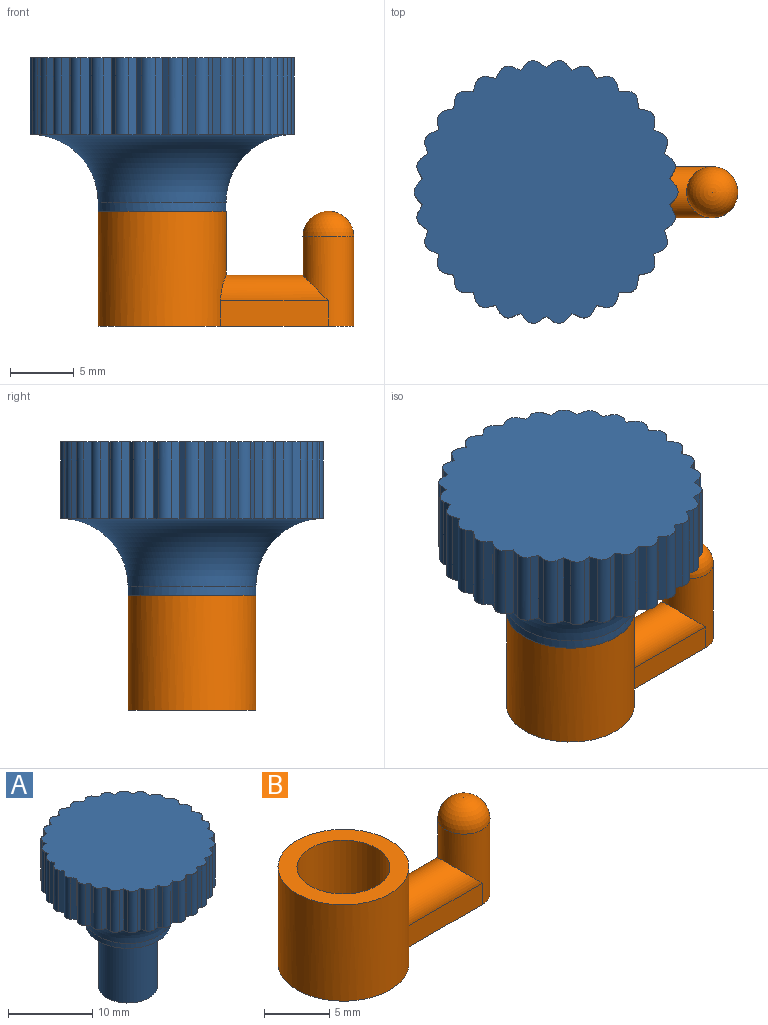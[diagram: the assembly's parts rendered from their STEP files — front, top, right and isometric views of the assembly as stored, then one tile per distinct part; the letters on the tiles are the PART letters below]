
ASSEMBLY  parts=2 mates=1
PART A: 133 faces, bbox 30.5x30.5x21 mm
  f0: cylinder r=5mm len=10mm, axis (0,0,-1), area 22mm2, adj f92,f93
  f1: plane 0.36x0.16mm, normal (0,0,-1), area 0mm2, adj f92,f122
  f2: plane 0.39x0.08mm, normal (0,0,-1), area 0mm2, adj f92,f123
  f3: plane 0.4x0.03mm, normal (0,0,-1), area 0mm2, adj f92,f124
  f4: plane 0.39x0.08mm, normal (0,0,-1), area 0mm2, adj f92,f125
  f5: plane 0.36x0.16mm, normal (0,0,-1), area 0mm2, adj f92,f126
  f6: plane 0.32x0.23mm, normal (0,0,-1), area 0mm2, adj f92,f127
  f7: plane 0.3x0.27mm, normal (0,0,-1), area 0mm2, adj f92,f128
  f8: plane 0.34x0.2mm, normal (0,0,-1), area 0mm2, adj f92,f129
  f9: plane 0.38x0.12mm, normal (0,0,-1), area 0mm2, adj f92,f130
  f10: plane 0.4x0.05mm, normal (0,0,-1), area 0mm2, adj f92,f131
  f11: plane 0.4x0.05mm, normal (0,0,-1), area 0mm2, adj f92,f132
  f12: plane 0.38x0.12mm, normal (0,0,-1), area 0mm2, adj f92,f103
  f13: plane 0.34x0.2mm, normal (0,0,-1), area 0mm2, adj f92,f104
  f14: plane 0.3x0.27mm, normal (0,0,-1), area 0mm2, adj f92,f105
  f15: plane 0.32x0.23mm, normal (0,0,-1), area 0mm2, adj f92,f106
  f16: plane 0.36x0.16mm, normal (0,0,-1), area 0mm2, adj f92,f107
  f17: plane 0.39x0.08mm, normal (0,0,-1), area 0mm2, adj f92,f108
  f18: plane 0.4x0.03mm, normal (0,0,-1), area 0mm2, adj f92,f109
  f19: plane 0.39x0.08mm, normal (0,0,-1), area 0mm2, adj f92,f110
  f20: plane 0.36x0.16mm, normal (0,0,-1), area 0mm2, adj f92,f111
  f21: plane 0.32x0.23mm, normal (0,0,-1), area 0mm2, adj f92,f112
  f22: plane 0.3x0.27mm, normal (0,0,-1), area 0mm2, adj f92,f113
  f23: plane 0.34x0.2mm, normal (0,0,-1), area 0mm2, adj f92,f114
  f24: plane 0.38x0.12mm, normal (0,0,-1), area 0mm2, adj f92,f115
  f25: plane 0.4x0.05mm, normal (0,0,-1), area 0mm2, adj f92,f116
  f26: plane 0.4x0.05mm, normal (0,0,-1), area 0mm2, adj f92,f117
  f27: plane 0.38x0.12mm, normal (0,0,-1), area 0mm2, adj f92,f118
  f28: plane 0.34x0.2mm, normal (0,0,-1), area 0mm2, adj f92,f119
  f29: plane 0.3x0.27mm, normal (0,0,-1), area 0mm2, adj f92,f120
  f30: plane 6.04x0.5mm, normal (-0.75,0.66,0), area 3.9mm2, adj f31,f90,f92,f132
  f31: plane 6.04x0.6mm, normal (0.42,0.91,0), area 3.9mm2, adj f30,f90,f92,f103
  f32: plane 6.04x0.57mm, normal (-0.87,0.49,0), area 3.9mm2, adj f33,f90,f92,f103
  f33: plane 6.04x0.64mm, normal (0.22,0.98,0), area 3.9mm2, adj f32,f90,f92,f104
  f34: plane 6.04x0.63mm, normal (-0.95,0.3,0), area 3.9mm2, adj f35,f90,f92,f104
  f35: plane 6.04x0.66mm, normal (0.01,1,0), area 3.9mm2, adj f34,f90,f92,f105
  f36: plane 6.04x0.65mm, normal (-1,0.09,0), area 3.9mm2, adj f37,f90,f92,f105
  f37: plane 6.04x0.65mm, normal (-0.2,0.98,0), area 3.9mm2, adj f36,f90,f92,f106
  f38: plane 6.04x0.65mm, normal (-0.99,-0.12,0), area 3.9mm2, adj f39,f90,f92,f106
  f39: plane 6.04x0.6mm, normal (-0.4,0.92,0), area 3.9mm2, adj f38,f90,f92,f107
  f40: plane 6.04x0.62mm, normal (-0.95,-0.32,0), area 3.9mm2, adj f41,f90,f92,f107
  f41: plane 6.04x0.54mm, normal (-0.58,0.82,0), area 3.9mm2, adj f40,f90,f92,f108
  f42: plane 6.04x0.57mm, normal (-0.86,-0.51,0), area 3.9mm2, adj f43,f90,f92,f108
  f43: plane 6.04x0.49mm, normal (-0.74,0.68,0), area 3.9mm2, adj f42,f90,f92,f109
  f44: plane 6.04x0.49mm, normal (-0.74,-0.68,0), area 3.9mm2, adj f45,f90,f92,f109
  f45: plane 6.04x0.57mm, normal (-0.86,0.51,0), area 3.9mm2, adj f44,f90,f92,f110
  f46: plane 6.04x0.54mm, normal (-0.58,-0.82,0), area 3.9mm2, adj f47,f90,f92,f110
  f47: plane 6.04x0.62mm, normal (-0.95,0.32,0), area 3.9mm2, adj f46,f90,f92,f111
  f48: plane 6.04x0.6mm, normal (-0.4,-0.92,0), area 3.9mm2, adj f49,f90,f92,f111
  f49: plane 6.04x0.65mm, normal (-0.99,0.12,0), area 3.9mm2, adj f48,f90,f92,f112
  f50: plane 6.04x0.65mm, normal (-0.2,-0.98,0), area 3.9mm2, adj f51,f90,f92,f112
  f51: plane 6.04x0.65mm, normal (-1,-0.09,0), area 3.9mm2, adj f50,f90,f92,f113
  f52: plane 6.04x0.66mm, normal (0.01,-1,0), area 3.9mm2, adj f53,f90,f92,f113
  f53: plane 6.04x0.63mm, normal (-0.95,-0.3,0), area 3.9mm2, adj f52,f90,f92,f114
  f54: plane 6.04x0.64mm, normal (0.22,-0.98,0), area 3.9mm2, adj f55,f90,f92,f114
  f55: plane 6.04x0.57mm, normal (-0.87,-0.49,0), area 3.9mm2, adj f54,f90,f92,f115
  f56: plane 6.04x0.6mm, normal (0.42,-0.91,0), area 3.9mm2, adj f57,f90,f92,f115
  f57: plane 6.04x0.5mm, normal (-0.75,-0.66,0), area 3.9mm2, adj f56,f90,f92,f116
  f58: plane 6.04x0.53mm, normal (0.6,-0.8,0), area 3.9mm2, adj f59,f90,f92,f116
  f59: plane 6.04x0.53mm, normal (-0.6,-0.8,0), area 3.9mm2, adj f58,f90,f92,f117
  f60: plane 6.04x0.5mm, normal (0.75,-0.66,0), area 3.9mm2, adj f61,f90,f92,f117
  f61: plane 6.04x0.6mm, normal (-0.42,-0.91,0), area 3.9mm2, adj f60,f90,f92,f118
  f62: plane 6.04x0.57mm, normal (0.87,-0.49,0), area 3.9mm2, adj f63,f90,f92,f118
  f63: plane 6.04x0.64mm, normal (-0.22,-0.98,0), area 3.9mm2, adj f62,f90,f92,f119
  f64: plane 6.04x0.63mm, normal (0.95,-0.3,0), area 3.9mm2, adj f65,f90,f92,f119
  f65: plane 6.04x0.66mm, normal (-0.01,-1,0), area 3.9mm2, adj f64,f90,f92,f120
  f66: plane 6.04x0.65mm, normal (1,-0.09,0), area 3.9mm2, adj f67,f90,f92,f120
  f67: plane 6.04x0.65mm, normal (0.2,-0.98,0), area 3.9mm2, adj f66,f90,f92,f121
  f68: plane 6.04x0.65mm, normal (0.99,0.12,0), area 3.9mm2, adj f69,f90,f92,f121
  f69: plane 6.04x0.6mm, normal (0.4,-0.92,0), area 3.9mm2, adj f68,f90,f92,f122
  f70: plane 6.04x0.62mm, normal (0.95,0.32,0), area 3.9mm2, adj f71,f90,f92,f122
  f71: plane 6.04x0.54mm, normal (0.58,-0.82,0), area 3.9mm2, adj f70,f90,f92,f123
  f72: plane 6.04x0.57mm, normal (0.86,0.51,0), area 3.9mm2, adj f73,f90,f92,f123
  f73: plane 6.04x0.49mm, normal (0.74,-0.68,0), area 3.9mm2, adj f72,f90,f92,f124
  f74: plane 6.04x0.49mm, normal (0.74,0.68,0), area 3.9mm2, adj f75,f90,f92,f124
  f75: plane 6.04x0.57mm, normal (0.86,-0.51,0), area 3.9mm2, adj f74,f90,f92,f125
  f76: plane 6.04x0.54mm, normal (0.58,0.82,0), area 3.9mm2, adj f77,f90,f92,f125
  f77: plane 6.04x0.62mm, normal (0.95,-0.32,0), area 3.9mm2, adj f76,f90,f92,f126
  f78: plane 6.04x0.6mm, normal (0.4,0.92,0), area 3.9mm2, adj f79,f90,f92,f126
  f79: plane 6.04x0.65mm, normal (0.99,-0.12,0), area 3.9mm2, adj f78,f90,f92,f127
  f80: plane 6.04x0.65mm, normal (0.2,0.98,0), area 3.9mm2, adj f81,f90,f92,f127
  f81: plane 6.04x0.65mm, normal (1,0.09,0), area 3.9mm2, adj f80,f90,f92,f128
  f82: plane 6.04x0.66mm, normal (-0.01,1,0), area 3.9mm2, adj f83,f90,f92,f128
  f83: plane 6.04x0.63mm, normal (0.95,0.3,0), area 3.9mm2, adj f82,f90,f92,f129
  f84: plane 6.04x0.64mm, normal (-0.22,0.98,0), area 3.9mm2, adj f85,f90,f92,f129
  f85: plane 6.04x0.57mm, normal (0.87,0.49,0), area 3.9mm2, adj f84,f90,f92,f130
  f86: plane 6.04x0.6mm, normal (-0.42,0.91,0), area 3.9mm2, adj f87,f90,f92,f130
  f87: plane 6.04x0.5mm, normal (0.75,0.66,0), area 3.9mm2, adj f86,f90,f92,f131
  f88: plane 6.04x0.53mm, normal (-0.6,0.8,0), area 3.9mm2, adj f89,f90,f92,f131
  f89: plane 6.04x0.53mm, normal (0.6,0.8,0), area 3.9mm2, adj f88,f90,f92,f132
  f90: plane 20.65x20.54mm, normal (0,0,1), area 320.3mm2, adj f30,f31,f32,f33,f34,f35,f36,f37
  f91: plane 0.32x0.23mm, normal (0,0,-1), area 0mm2, adj f92,f121
  f92: torus R=10.3mm, axis (0,0,1), area 349.2mm2, adj f0,f1,f2,f3,f4,f5,f6,f7
  f93: plane 10x10mm, normal (0,0,-1), area 40.1mm2, adj f0,f94
  f94: cylinder r=3.5mm len=9mm, axis (0,0,1), area 197.9mm2, adj f93,f95
  f95: plane 7x7mm, normal (0,0,-1), area 27.8mm2, adj f94,f96,f97,f98,f99,f100,f101
  f96: plane 10x1.76mm, normal (-0.87,0.5,0), area 20.3mm2, adj f95,f97,f101,f102
  f97: plane 10x2.03mm, normal (0,1,0), area 20.3mm2, adj f95,f96,f98,f102
  f98: plane 10x1.76mm, normal (0.87,0.5,0), area 20.3mm2, adj f95,f97,f99,f102
  f99: plane 10x1.76mm, normal (0.87,-0.5,0), area 20.3mm2, adj f95,f98,f100,f102
  f100: plane 10x2.03mm, normal (0,-1,0), area 20.3mm2, adj f95,f99,f101,f102
  f101: plane 10x1.76mm, normal (-0.87,-0.5,0), area 20.3mm2, adj f95,f96,f100,f102
  f102: plane 4.06x3.51mm, normal (0,0,-1), area 10.7mm2, adj f96,f97,f98,f99,f100,f101
  f103: cylinder r=0.8mm len=6mm, axis (0,0,-1), area 7.1mm2, adj f12,f31,f32,f90,f92
  f104: cylinder r=0.8mm len=6mm, axis (0,0,-1), area 7.1mm2, adj f13,f33,f34,f90,f92
  f105: cylinder r=0.8mm len=6mm, axis (0,0,-1), area 7.1mm2, adj f14,f35,f36,f90,f92
  f106: cylinder r=0.8mm len=6mm, axis (0,0,-1), area 7.1mm2, adj f15,f37,f38,f90,f92
  f107: cylinder r=0.8mm len=6mm, axis (0,0,-1), area 7.1mm2, adj f16,f39,f40,f90,f92
  f108: cylinder r=0.8mm len=6mm, axis (0,0,-1), area 7.1mm2, adj f17,f41,f42,f90,f92
  f109: cylinder r=0.8mm len=6mm, axis (0,0,-1), area 7.1mm2, adj f18,f43,f44,f90,f92
  f110: cylinder r=0.8mm len=6mm, axis (0,0,-1), area 7.1mm2, adj f19,f45,f46,f90,f92
  f111: cylinder r=0.8mm len=6mm, axis (0,0,-1), area 7.1mm2, adj f20,f47,f48,f90,f92
  f112: cylinder r=0.8mm len=6mm, axis (0,0,-1), area 7.1mm2, adj f21,f49,f50,f90,f92
  f113: cylinder r=0.8mm len=6mm, axis (0,0,-1), area 7.1mm2, adj f22,f51,f52,f90,f92
  f114: cylinder r=0.8mm len=6mm, axis (0,0,-1), area 7.1mm2, adj f23,f53,f54,f90,f92
  f115: cylinder r=0.8mm len=6mm, axis (0,0,-1), area 7.1mm2, adj f24,f55,f56,f90,f92
  f116: cylinder r=0.8mm len=6mm, axis (0,0,-1), area 7.1mm2, adj f25,f57,f58,f90,f92
  f117: cylinder r=0.8mm len=6mm, axis (0,0,-1), area 7.1mm2, adj f26,f59,f60,f90,f92
  f118: cylinder r=0.8mm len=6mm, axis (0,0,-1), area 7.1mm2, adj f27,f61,f62,f90,f92
  f119: cylinder r=0.8mm len=6mm, axis (0,0,-1), area 7.1mm2, adj f28,f63,f64,f90,f92
  f120: cylinder r=0.8mm len=6mm, axis (0,0,-1), area 7.1mm2, adj f29,f65,f66,f90,f92
  f121: cylinder r=0.8mm len=6mm, axis (0,0,-1), area 7.1mm2, adj f67,f68,f90,f91,f92
  f122: cylinder r=0.8mm len=6mm, axis (0,0,-1), area 7.1mm2, adj f1,f69,f70,f90,f92
  f123: cylinder r=0.8mm len=6mm, axis (0,0,-1), area 7.1mm2, adj f2,f71,f72,f90,f92
  f124: cylinder r=0.8mm len=6mm, axis (0,0,-1), area 7.1mm2, adj f3,f73,f74,f90,f92
  f125: cylinder r=0.8mm len=6mm, axis (0,0,-1), area 7.1mm2, adj f4,f75,f76,f90,f92
  f126: cylinder r=0.8mm len=6mm, axis (0,0,-1), area 7.1mm2, adj f5,f77,f78,f90,f92
  f127: cylinder r=0.8mm len=6mm, axis (0,0,-1), area 7.1mm2, adj f6,f79,f80,f90,f92
  f128: cylinder r=0.8mm len=6mm, axis (0,0,-1), area 7.1mm2, adj f7,f81,f82,f90,f92
  f129: cylinder r=0.8mm len=6mm, axis (0,0,-1), area 7.1mm2, adj f8,f83,f84,f90,f92
  f130: cylinder r=0.8mm len=6mm, axis (0,0,-1), area 7.1mm2, adj f9,f85,f86,f90,f92
  f131: cylinder r=0.8mm len=6mm, axis (0,0,-1), area 7.1mm2, adj f10,f87,f88,f90,f92
  f132: cylinder r=0.8mm len=6mm, axis (0,0,-1), area 7.1mm2, adj f11,f30,f89,f90,f92
PART B: 9 faces, bbox 20x10x9 mm
  f0: cylinder r=5mm len=10mm, axis (0,0,-1), area 268.1mm2, adj f1,f2,f3,f5,f7
  f1: plane 20x10mm, normal (0,0,-1), area 77.8mm2, adj f0,f2,f3,f4,f8
  f2: plane 8.42x2mm, normal (0,-1,0), area 16.8mm2, adj f0,f1,f4,f5
  f3: plane 8.42x2mm, normal (0,1,0), area 16.8mm2, adj f0,f1,f4,f5
  f4: cylinder r=2mm len=7mm, axis (0,0,1), area 67.4mm2, adj f1,f2,f3,f5,f6
  f5: cylinder r=2mm len=8.42mm, axis (1,0,0), area 43.6mm2, adj f0,f2,f3,f4
  f6: sphere r=2mm, area 25.1mm2, adj f4
  f7: plane 10x10mm, normal (0,0,1), area 38.9mm2, adj f0,f8
  f8: cylinder r=3.55mm len=9mm, axis (0,0,1), area 200.7mm2, adj f1,f7
PLACE A t=(-7.57,-1.56,-4.61)mm
PLACE B t=(-7.57,-1.56,-4.61)mm
MATE slider A.f94 <-> B.f8  axis (0,0,1) through (-7.57,-1.56,-4.61)mm
